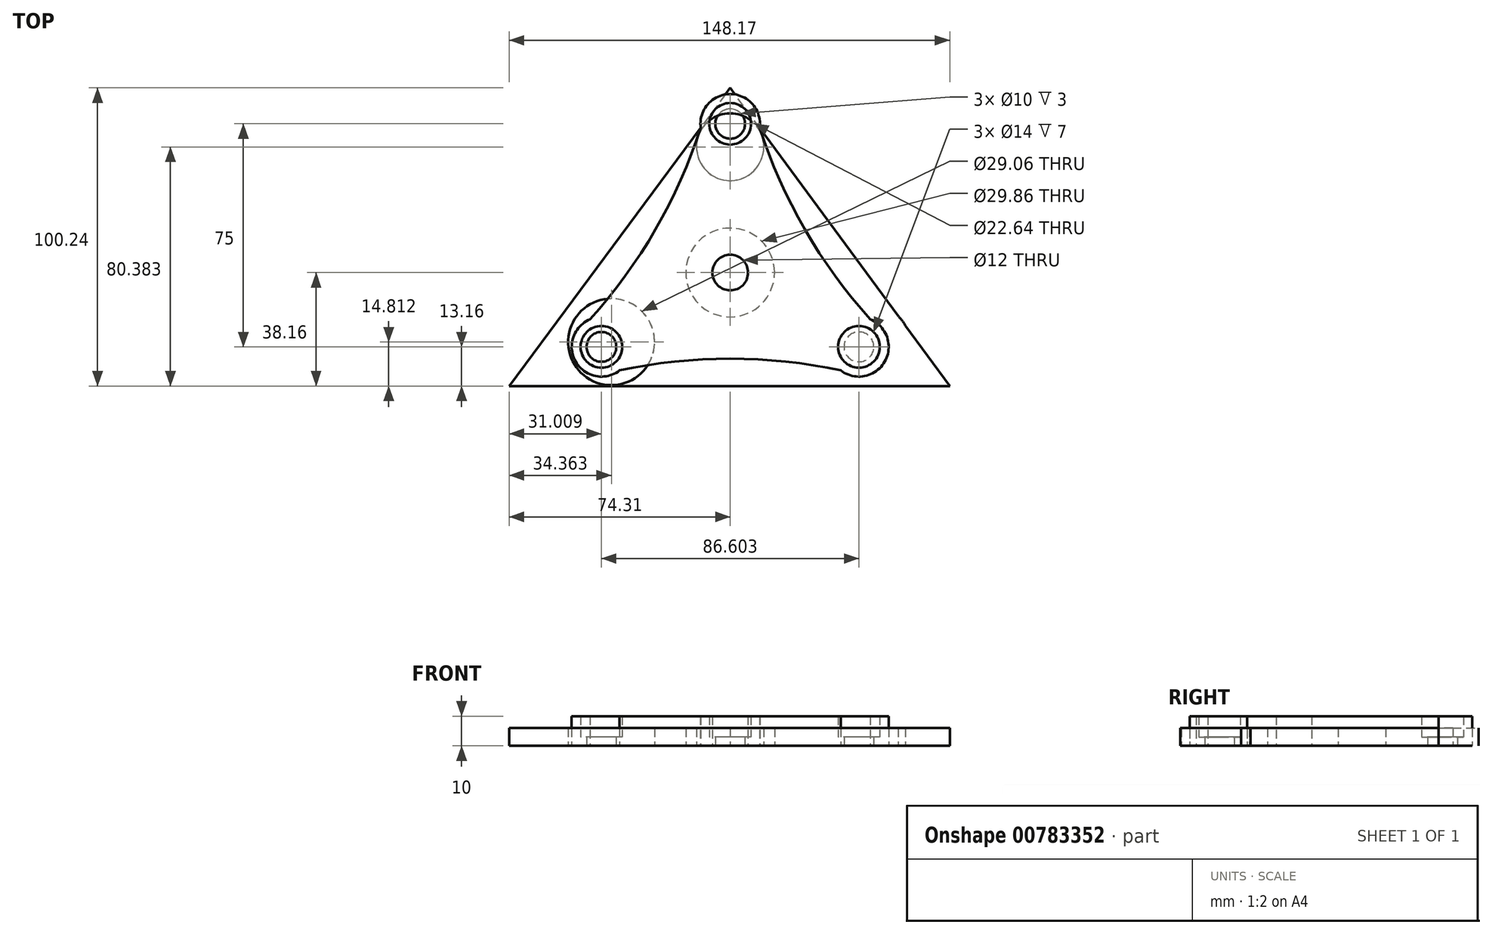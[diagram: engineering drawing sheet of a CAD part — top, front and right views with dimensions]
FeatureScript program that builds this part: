
annotation { "Feature Type Name" : "Feature", "Feature Type Description" : "" }
export const myFeature = defineFeature(function(context is Context, id is Id, definition is map)
    precondition{}
    {
        {
            var Q0;
            Q0=qCreatedBy(makeId("Top.planeOp"),FACE);
            var sketch = newSketch(context, id + "F0", { "sketchPlane" : qUnion([Q0])});
            skLineSegment(sketch, "E0", {"start": v(-49.7, 0) * mm, "end": v(39, 0) * mm});
            skLineSegment(sketch, "E1", {"start": v(0, 62.08) * mm, "end": v(-74.3, -38.16) * mm});
            skLineSegment(sketch, "E2", {"start": v(-74.3, -38.16) * mm, "end": v(73.86, -38.16) * mm});
            skLineSegment(sketch, "E3", {"start": v(73.86, -38.16) * mm, "end": v(0, 62.08) * mm});
            skCircle(sketch, "E4", {"center": v(0, 0) * mm, "radius": 14.93 * mm});
            skCircle(sketch, "E5", {"center": v(0, 42.22) * mm, "radius": 11.32 * mm});
            skCircle(sketch, "E6", {"center": v(-39.95, -23.35) * mm, "radius": 14.53 * mm});
            skCircle(sketch, "E7", {"center": v(46.75, -24.3) * mm, "radius": 13.74 * mm});
            skSolve(sketch);
        }
        {
            var Q0;
            Q0=qCreatedBy(makeId("Top.planeOp"),FACE);
            var sketch = newSketch(context, id + "F1", { "sketchPlane" : qUnion([Q0])});
            skCircle(sketch, "E8.cCircle", {"center": v(0, 0) * mm, "radius": 32.92 * mm, "construction": true});
            skLineSegment(sketch, "E8.0", {"start": v(57.01, -32.92) * mm, "end": v(-57.01, -32.92) * mm, "construction": true});
            skLineSegment(sketch, "E8.1", {"start": v(-57.01, -32.92) * mm, "end": v(0, 65.83) * mm, "construction": true});
            skLineSegment(sketch, "E8.2", {"start": v(0, 65.83) * mm, "end": v(57.01, -32.92) * mm, "construction": true});
            skPoint(sketch, "E8.0.midPoint", {"position": v(0, -32.92) * mm});
            skCircle(sketch, "E9", {"center": v(0, 50) * mm, "radius": 7 * mm});
            skLineSegment(sketch, "E10", {"start": v(0, 0) * mm, "end": v(0, 50) * mm, "construction": true});
            skCircle(sketch, "E11", {"center": v(0, 50) * mm, "radius": 5 * mm});
            skArc(sketch, "E12", {"start": v(-9.91, 48.67) * mm, "mid": v(0, 60) * mm, "end": v(9.91, 48.67) * mm});
            skLineSegment(sketch, "E13", {"start": v(-28.5, 16.46) * mm, "end": v(-179.34, 103.54) * mm, "construction": true});
            skArc(sketch, "E14", {"start": v(-47.1, -15.75) * mm, "mid": v(-25.1, 14.5) * mm, "end": v(-9.91, 48.67) * mm});
            skLineSegment(sketch, "E15.1.0", {"start": v(0, 0) * mm, "end": v(-43.3, -25) * mm, "construction": true});
            skArc(sketch, "E15.1.1", {"start": v(37.2, -32.92) * mm, "mid": v(0, -28.99) * mm, "end": v(-37.2, -32.92) * mm});
            skArc(sketch, "E15.1.2", {"start": v(-37.2, -32.92) * mm, "mid": v(-51.96, -30) * mm, "end": v(-47.1, -15.75) * mm});
            skCircle(sketch, "E15.1.3", {"center": v(-43.3, -25) * mm, "radius": 7 * mm});
            skCircle(sketch, "E15.1.4", {"center": v(-43.3, -25) * mm, "radius": 5 * mm});
            skLineSegment(sketch, "E15.2.0", {"start": v(0, 0) * mm, "end": v(43.3, -25) * mm, "construction": true});
            skArc(sketch, "E15.2.1", {"start": v(9.91, 48.67) * mm, "mid": v(25.1, 14.5) * mm, "end": v(47.1, -15.75) * mm});
            skArc(sketch, "E15.2.2", {"start": v(47.1, -15.75) * mm, "mid": v(51.96, -30) * mm, "end": v(37.2, -32.92) * mm});
            skCircle(sketch, "E15.2.3", {"center": v(43.3, -25) * mm, "radius": 7 * mm});
            skCircle(sketch, "E15.2.4", {"center": v(43.3, -25) * mm, "radius": 5 * mm});
            skPoint(sketch, "E16", {"position": v(0, 57) * mm});
            skPoint(sketch, "E17", {"position": v(-103.92, 60) * mm});
            skPoint(sketch, "E18", {"position": v(-86.6, 50) * mm});
            skCircle(sketch, "E19", {"center": v(0, 0) * mm, "radius": 6 * mm});
            skSolve(sketch);
        }
        {
            var Q0;
            Q0=makeQuery(id+"F1.imprint","IMPRINT",FACE,{"disambiguationData":[TD([[makeQuery(id+"F1.imprint","IMPRINT",EDGE,{"derivedFrom":sQuery(id+"F1.wireOp",EDGE,"E9")}),-1.0]])]});
            var Q1;
            Q1=makeQuery(id+"F1.imprint","IMPRINT",FACE,{"disambiguationData":[TD([[makeQuery(id+"F1.imprint","IMPRINT",EDGE,{"derivedFrom":sQuery(id+"F1.wireOp",EDGE,"E15.1.3")}),1.0]])]});
            var Q2;
            Q2=makeQuery(id+"F1.imprint","IMPRINT",FACE,{"disambiguationData":[TD([[makeQuery(id+"F1.imprint","IMPRINT",EDGE,{"derivedFrom":sQuery(id+"F1.wireOp",EDGE,"E15.2.3")}),1.0]])]});
            var Q3;
            Q3=makeQuery(id+"F1.imprint","IMPRINT",FACE,{"disambiguationData":[TD([[makeQuery(id+"F1.imprint","IMPRINT",EDGE,{"derivedFrom":sQuery(id+"F1.wireOp",EDGE,"E9")}),1.0]])]});
            extrude(context, id + "F2", {"entities" : qUnion([Q0, Q1, Q2, Q3]), "depth" : 3 * mm, "offsetDistance" : 25 * mm});
        }
        {
            var Q0;
            Q0=makeQuery(id+"F1.imprint","IMPRINT",FACE,{"disambiguationData":[TD([[makeQuery(id+"F1.imprint","IMPRINT",EDGE,{"derivedFrom":sQuery(id+"F1.wireOp",EDGE,"E9")}),-1.0]])]});
            extrude(context, id + "F3", {"entities" : qUnion([Q0]), "operationType" : NewBodyOperationType.ADD, "depth" : 10 * mm, "offsetDistance" : 25 * mm});
        }
        {
            var Q0;
            Q0=qSketchRegion(id+"F0",true);
            extrude(context, id + "F4", {"entities" : qUnion([Q0]), "depth" : 6 * mm, "offsetDistance" : 25 * mm});
        }
        {
            var Q0;
            Q0=sQuery(id+"F0.wireOp",EDGE,"E7");
            extrude(context, id + "F5", {"bodyType" : ToolBodyType.SURFACE, "surfaceEntities" : qUnion([Q0]), "depth" : 6 * mm, "offsetDistance" : 25 * mm});
        }
    });
